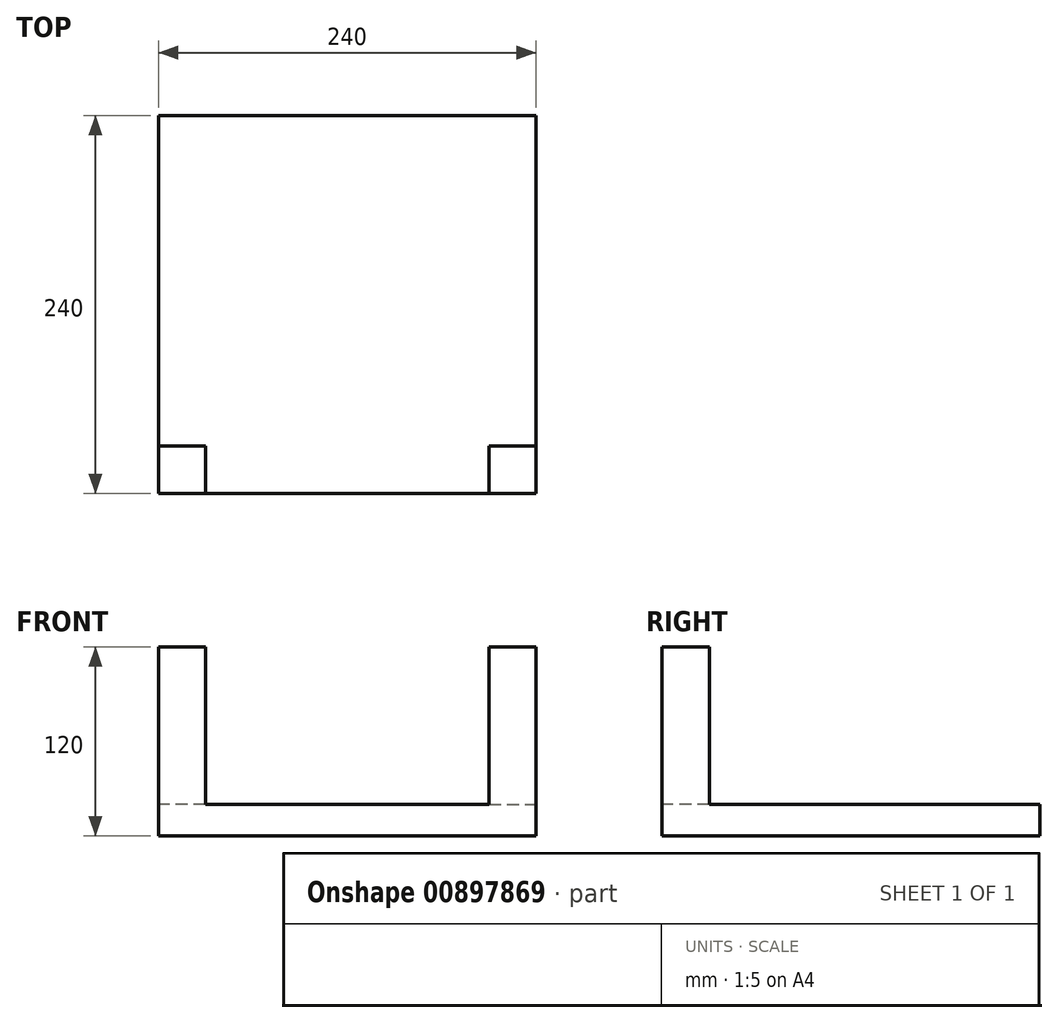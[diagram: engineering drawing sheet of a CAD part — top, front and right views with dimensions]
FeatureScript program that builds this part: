
annotation { "Feature Type Name" : "Feature", "Feature Type Description" : "" }
export const myFeature = defineFeature(function(context is Context, id is Id, definition is map)
    precondition{}
    {
        {
            var Q0;
            Q0=qCreatedBy(makeId("Top.planeOp"),FACE);
            var sketch = newSketch(context, id + "F0", { "sketchPlane" : qUnion([Q0])});
            skLineSegment(sketch, "E0.bottom", {"start": v(-120, 120) * mm, "end": v(120, 120) * mm});
            skLineSegment(sketch, "E0.top", {"start": v(-120, -120) * mm, "end": v(120, -120) * mm});
            skLineSegment(sketch, "E0.left", {"start": v(-120, 120) * mm, "end": v(-120, -120) * mm});
            skLineSegment(sketch, "E0.right", {"start": v(120, 120) * mm, "end": v(120, -120) * mm});
            skSolve(sketch);
        }
        {
            var Q0;
            Q0 = qSketchRegion(id + "F0", true);
            extrude(context, id + "F1", {"entities" : qUnion([Q0]), "depth" : 20 * mm, "offsetDistance" : 25 * mm});
        }
        {
            var Q0;
            Q0=makeQuery(id+"F1.opExtrude","CAP_FACE",FACE,{"disambiguationData":[OSD([sQuery(id+"F0.wireOp",EDGE,"E0.bottom"),sQuery(id+"F0.wireOp",EDGE,"E0.top"),sQuery(id+"F0.wireOp",EDGE,"E0.left"),sQuery(id+"F0.wireOp",EDGE,"E0.right")])],"isStart":false});
            var sketch = newSketch(context, id + "F2", { "sketchPlane" : qUnion([Q0])});
            skLineSegment(sketch, "E1.bottom", {"start": v(90, -90) * mm, "end": v(120, -90) * mm});
            skLineSegment(sketch, "E1.top", {"start": v(90, -120) * mm, "end": v(120, -120) * mm});
            skLineSegment(sketch, "E1.left", {"start": v(90, -90) * mm, "end": v(90, -120) * mm});
            skLineSegment(sketch, "E1.right", {"start": v(120, -90) * mm, "end": v(120, -120) * mm});
            skLineSegment(sketch, "E2.MirrorCS", {"start": v(-90, -90) * mm, "end": v(-120, -90) * mm});
            skLineSegment(sketch, "E3.MirrorCS", {"start": v(-90, -90) * mm, "end": v(-90, -120) * mm});
            skLineSegment(sketch, "E4.MirrorCS", {"start": v(-90, -120) * mm, "end": v(-120, -120) * mm});
            skLineSegment(sketch, "E5.MirrorCS", {"start": v(-120, -90) * mm, "end": v(-120, -120) * mm});
            skSolve(sketch);
        }
        {
            var Q0;
            Q0=makeQuery(id+"F2.imprint","IMPRINT",FACE,{"disambiguationData":[TD([[makeQuery(id+"F2.imprint","IMPRINT",EDGE,{"derivedFrom":sQuery(id+"F2.wireOp",EDGE,"E1.bottom")}),-1.0]])]});
            var Q1;
            Q1=makeQuery(id+"F2.imprint","IMPRINT",FACE,{"disambiguationData":[TD([[makeQuery(id+"F2.imprint","IMPRINT",EDGE,{"derivedFrom":sQuery(id+"F2.wireOp",EDGE,"E2.MirrorCS")}),1.0]])]});
            extrude(context, id + "F3", {"entities" : qUnion([Q0, Q1]), "operationType" : NewBodyOperationType.ADD, "depth" : 100 * mm, "offsetDistance" : 25 * mm});
        }
    });
